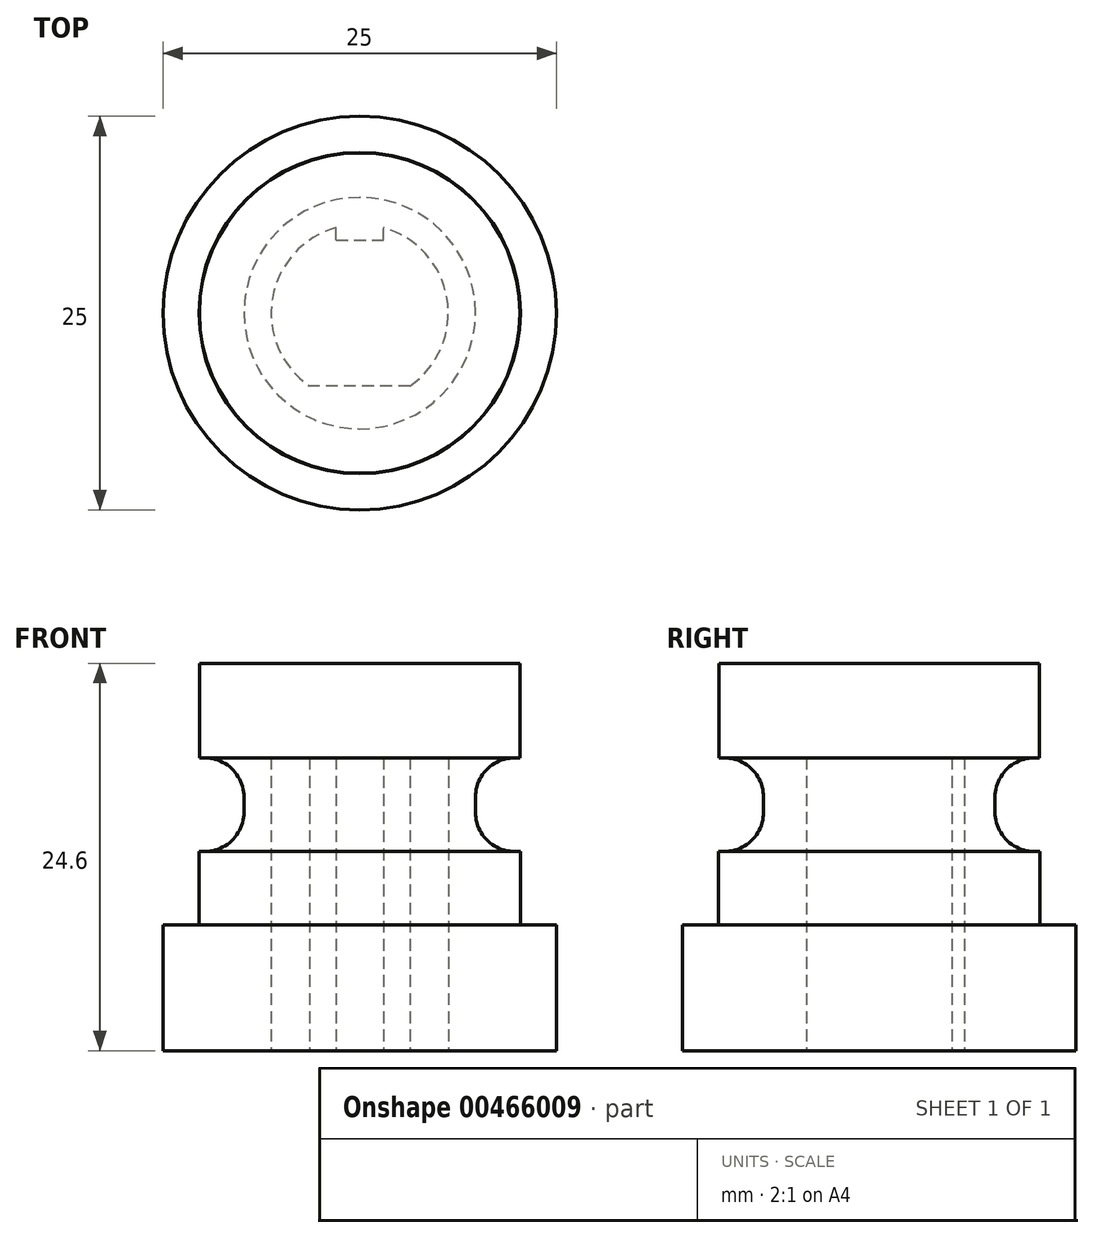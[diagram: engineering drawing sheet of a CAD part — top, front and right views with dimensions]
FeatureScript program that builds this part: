
annotation { "Feature Type Name" : "Feature", "Feature Type Description" : "" }
export const myFeature = defineFeature(function(context is Context, id is Id, definition is map)
    precondition{}
    {
        {
            var Q0;
            Q0=qCreatedBy(makeId("Top.planeOp"),FACE);
            var sketch = newSketch(context, id + "F0", { "sketchPlane" : qUnion([Q0])});
            skArc(sketch, "E0", {"start": v(3.2, -4.62) * mm, "mid": v(5.55, 0.94) * mm, "end": v(1.5, 5.42) * mm});
            skCircle(sketch, "E1", {"center": v(0, 0) * mm, "radius": 12.5 * mm});
            skCircle(sketch, "E2", {"center": v(0, 0) * mm, "radius": 10.2 * mm});
            skCircle(sketch, "E3", {"center": v(0, 0) * mm, "radius": 7.35 * mm});
            skLineSegment(sketch, "E4", {"start": v(3.2, -4.62) * mm, "end": v(-3.2, -4.62) * mm});
            skPoint(sketch, "E5.endSnap0", {"position": v(0, 5.63) * mm});
            skLineSegment(sketch, "E6", {"start": v(-1.5, 4.62) * mm, "end": v(1.5, 4.62) * mm});
            skLineSegment(sketch, "E7", {"start": v(-1.5, 4.62) * mm, "end": v(-1.5, 5.42) * mm});
            skLineSegment(sketch, "E8", {"start": v(1.5, 4.62) * mm, "end": v(1.5, 5.42) * mm});
            skArc(sketch, "E9.trimOffspring", {"start": v(-1.5, 5.42) * mm, "mid": v(-5.55, 0.94) * mm, "end": v(-3.2, -4.62) * mm});
            skSolve(sketch);
        }
        {
            var Q0;
            Q0=makeQuery(id+"F0.imprint","IMPRINT",FACE,{"disambiguationData":[TD([[makeQuery(id+"F0.imprint","IMPRINT",EDGE,{"derivedFrom":sQuery(id+"F0.wireOp",EDGE,"E1")}),1.0]])]});
            var Q1;
            Q1=makeQuery(id+"F0.imprint","IMPRINT",FACE,{"disambiguationData":[TD([[makeQuery(id+"F0.imprint","IMPRINT",EDGE,{"derivedFrom":sQuery(id+"F0.wireOp",EDGE,"E0")}),-1.0]])]});
            var Q2;
            Q2=makeQuery(id+"F0.imprint","IMPRINT",FACE,{"disambiguationData":[TD([[makeQuery(id+"F0.imprint","IMPRINT",EDGE,{"derivedFrom":sQuery(id+"F0.wireOp",EDGE,"E2")}),1.0]])]});
            extrude(context, id + "F1", {"entities" : qUnion([Q0, Q1, Q2]), "depth" : 8 * mm});
        }
        {
            var Q0;
            Q0=makeQuery(id+"F0.imprint","IMPRINT",FACE,{"disambiguationData":[TD([[makeQuery(id+"F0.imprint","IMPRINT",EDGE,{"derivedFrom":sQuery(id+"F0.wireOp",EDGE,"E0")}),-1.0]])]});
            var Q1;
            Q1=makeQuery(id+"F0.imprint","IMPRINT",FACE,{"disambiguationData":[TD([[makeQuery(id+"F0.imprint","IMPRINT",EDGE,{"derivedFrom":sQuery(id+"F0.wireOp",EDGE,"E2")}),1.0]])]});
            extrude(context, id + "F2", {"entities" : qUnion([Q0, Q1]), "operationType" : NewBodyOperationType.ADD, "depth" : 12.65 * mm});
        }
        {
            var Q0;
            Q0=makeQuery(id+"F0.imprint","IMPRINT",FACE,{"disambiguationData":[TD([[makeQuery(id+"F0.imprint","IMPRINT",EDGE,{"derivedFrom":sQuery(id+"F0.wireOp",EDGE,"E0")}),-1.0]])]});
            extrude(context, id + "F3", {"entities" : qUnion([Q0]), "operationType" : NewBodyOperationType.ADD, "depth" : 18.6 * mm});
        }
        {
            var Q0;
            Q0=makeQuery(id+"F3.opExtrude","CAP_FACE",FACE,{"disambiguationData":[OSD([sQuery(id+"F0.wireOp",EDGE,"E0"),sQuery(id+"F0.wireOp",EDGE,"E3")])],"isStart":false});
            var sketch = newSketch(context, id + "F4", { "sketchPlane" : qUnion([Q0])});
            skCircle(sketch, "E10", {"center": v(0, 0) * mm, "radius": 10.18 * mm});
            skSolve(sketch);
        }
        {
            var Q0;
            Q0 = qSketchRegion(id + "F4", true);
            extrude(context, id + "F5", {"entities" : qUnion([Q0]), "operationType" : NewBodyOperationType.ADD, "depth" : 6 * mm});
        }
        {
            var Q0;
            Q0=makeQuery(id+"F3.boolean.opBoolean","INTERSECT",EDGE,{"derivedFrom":[makeQuery(id+"F2.opExtrude","CAP_FACE",FACE,{"disambiguationData":[OSD([sQuery(id+"F0.wireOp",EDGE,"E0"),sQuery(id+"F0.wireOp",EDGE,"E2")])],"isStart":false}),makeQuery(id+"F3.opExtrude","SWEPT_FACE",FACE,{"disambiguationData":[OSD([sQuery(id+"F0.wireOp",EDGE,"E3")])]})]});
            fillet(context, id + "F6", {"entities" : qUnion([Q0]), "radius" : 2.5 * mm, "tangentPropagation" : true, "allowEdgeOverflow" : false});
        }
        {
            var Q0;
            Q0=makeQuery(id+"F3.opExtrude","CAP_EDGE",EDGE,{"disambiguationData":[OSD([sQuery(id+"F0.wireOp",EDGE,"E3")])],"isStart":false});
            fillet(context, id + "F7", {"entities" : qUnion([Q0]), "radius" : 2.5 * mm, "tangentPropagation" : true, "allowEdgeOverflow" : false});
        }
    });
